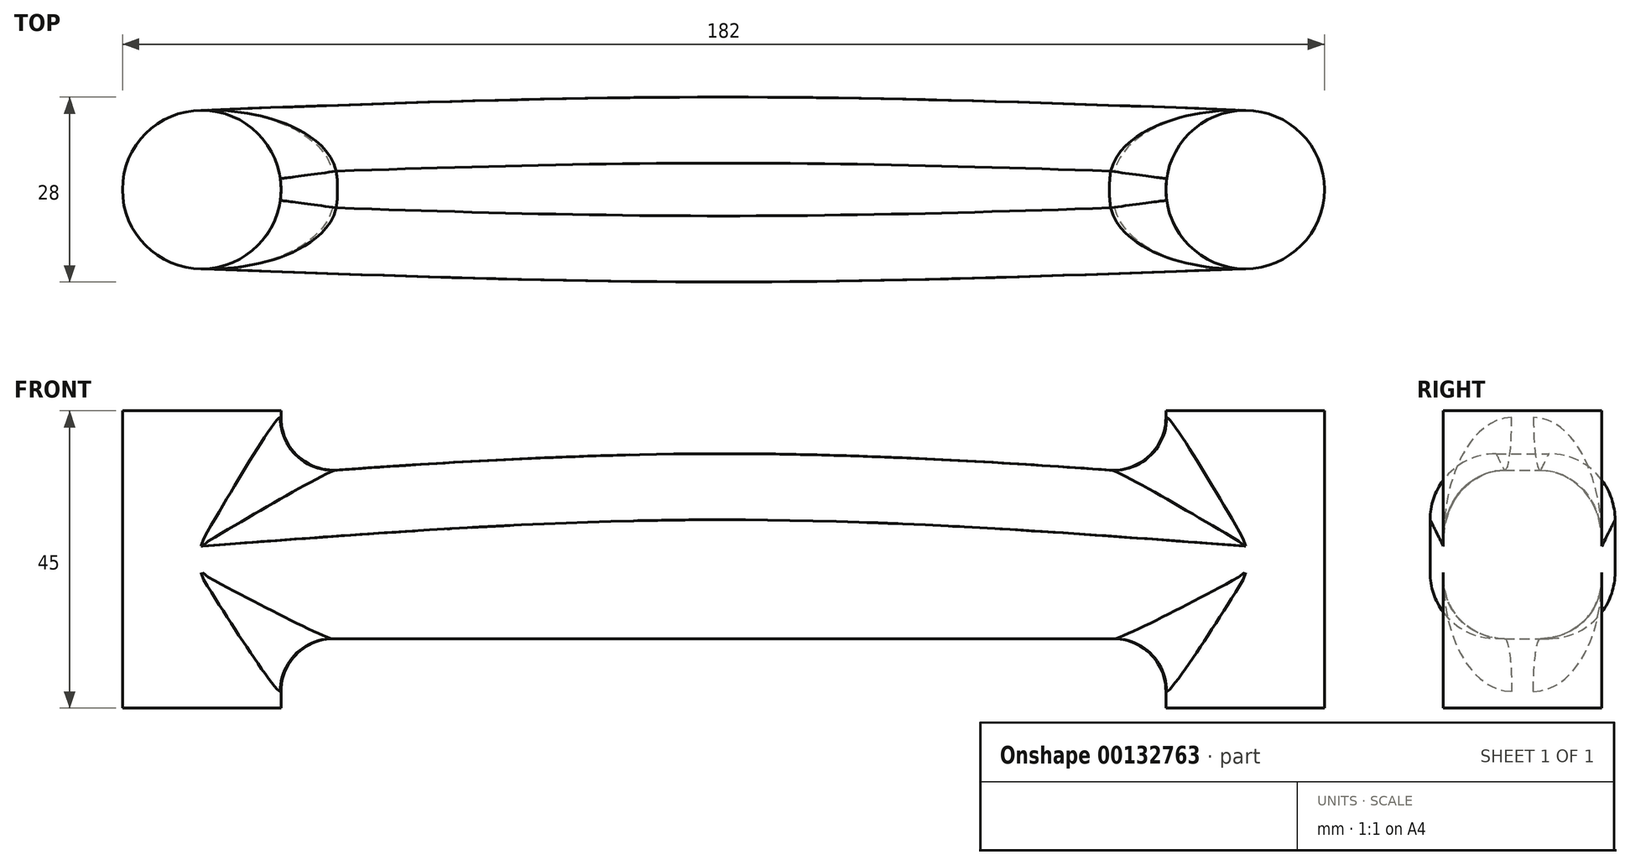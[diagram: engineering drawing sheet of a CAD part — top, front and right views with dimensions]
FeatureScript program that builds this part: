
annotation { "Feature Type Name" : "Feature", "Feature Type Description" : "" }
export const myFeature = defineFeature(function(context is Context, id is Id, definition is map)
    precondition{}
    {
        {
            var Q0;
            Q0=qCreatedBy(makeId("Top.planeOp"),FACE);
            var sketch = newSketch(context, id + "F0", { "sketchPlane" : qUnion([Q0])});
            skCircle(sketch, "E0", {"center": v(79, 0) * mm, "radius": 12 * mm});
            skLineSegment(sketch, "E1", {"start": v(-79, 0) * mm, "end": v(79, 0) * mm, "construction": true});
            skSolve(sketch);
        }
        {
            var Q0;
            Q0=makeQuery(id+"F0.imprint","IMPRINT",FACE,{"disambiguationData":[TD([[makeQuery(id+"F0.imprint","IMPRINT",EDGE,{"derivedFrom":sQuery(id+"F0.wireOp",EDGE,"6btjqJFc-xtUv-p354-ct1m-dMCtlRu3DlYN")}),1.0]])]});
            var Q1;
            Q1=makeQuery(id+"F0.imprint","IMPRINT",FACE,{"disambiguationData":[TD([[makeQuery(id+"F0.imprint","IMPRINT",EDGE,{"derivedFrom":sQuery(id+"F0.wireOp",EDGE,"E0")}),1.0]])]});
            extrude(context, id + "F1", {"entities" : qUnion([Q0, Q1]), "depth" : 45 * mm});
        }
        {
            var Q0;
            Q0=qCreatedBy(makeId("Right.planeOp"),FACE);
            cPlane(context, id + "F2", {"entities" : qUnion([Q0]), "cplaneType" : CPlaneType.OFFSET, "offset" : (158 / 2) * mm, "width" : 150 * mm, "height" : 150 * mm});
        }
        {
            var Q0;
            Q0=qCreatedBy(id+"F2.planeOp",FACE);
            var sketch = newSketch(context, id + "F3", { "sketchPlane" : qUnion([Q0])});
            skLineSegment(sketch, "E2.bottom", {"start": v(-12, 34.5) * mm, "end": v(12, 34.5) * mm});
            skLineSegment(sketch, "E2.top", {"start": v(-12, 10.5) * mm, "end": v(12, 10.5) * mm});
            skLineSegment(sketch, "E2.left", {"start": v(-12, 34.5) * mm, "end": v(-12, 10.5) * mm});
            skLineSegment(sketch, "E2.right", {"start": v(12, 34.5) * mm, "end": v(12, 10.5) * mm});
            skLineSegment(sketch, "E3", {"start": v(0, 10.5) * mm, "end": v(0, 0) * mm});
            skSolve(sketch);
        }
        {
            var Q0;
            Q0=qCreatedBy(makeId("Right.planeOp"),FACE);
            var sketch = newSketch(context, id + "F4", { "sketchPlane" : qUnion([Q0])});
            skLineSegment(sketch, "E4.bottom", {"start": v(-14, 38.5) * mm, "end": v(14, 38.5) * mm});
            skLineSegment(sketch, "E4.top", {"start": v(-14, 10.5) * mm, "end": v(14, 10.5) * mm});
            skLineSegment(sketch, "E4.left", {"start": v(-14, 38.5) * mm, "end": v(-14, 10.5) * mm});
            skLineSegment(sketch, "E4.right", {"start": v(14, 38.5) * mm, "end": v(14, 10.5) * mm});
            skLineSegment(sketch, "E5", {"start": v(0, 10.5) * mm, "end": v(0, 0) * mm});
            skSolve(sketch);
        }
        {
            var Q1;
            Q1=makeQuery(id+"F4.imprint","IMPRINT",FACE,{"disambiguationData":[TD([[makeQuery(id+"F4.imprint","IMPRINT",EDGE,{"derivedFrom":sQuery(id+"F4.wireOp",EDGE,"E4.bottom")}),-1.0]])]});
            var Q2;
            Q2=makeQuery(id+"F3.imprint","IMPRINT",FACE,{"disambiguationData":[TD([[makeQuery(id+"F3.imprint","IMPRINT",EDGE,{"derivedFrom":sQuery(id+"F3.wireOp",EDGE,"E2.bottom")}),-1.0]])]});
            loft(context, id + "F5", {"operationType" : NewBodyOperationType.ADD, "startCondition" : LoftEndDerivativeType.NORMAL_TO_PROFILE, "startMagnitude" : 1, "sheetProfilesArray" : [{ "sheetProfileEntities" : qUnion([Q1]) }, { "sheetProfileEntities" : qUnion([Q2]) }]});
        }
        {
            var Q0;
            Q0=makeQuery(id+"F5.opLoft","SWEPT_EDGE",EDGE,{"disambiguationData":[OSD([sQuery(id+"F3.wireOp",EDGE,"E2.bottom"),sQuery(id+"F3.wireOp",EDGE,"E2.right"),sQuery(id+"F4.wireOp",EDGE,"E4.bottom"),sQuery(id+"F4.wireOp",EDGE,"E4.right")])]});
            var Q1;
            Q1=makeQuery(id+"F5.opLoft","SWEPT_EDGE",EDGE,{"disambiguationData":[OSD([sQuery(id+"F3.wireOp",EDGE,"E2.bottom"),sQuery(id+"F3.wireOp",EDGE,"E2.left"),sQuery(id+"F4.wireOp",EDGE,"E4.bottom"),sQuery(id+"F4.wireOp",EDGE,"E4.left")])]});
            var Q2;
            Q2=makeQuery(id+"F5.opLoft","SWEPT_EDGE",EDGE,{"disambiguationData":[OSD([sQuery(id+"F3.wireOp",EDGE,"E2.top"),sQuery(id+"F3.wireOp",EDGE,"E2.right"),sQuery(id+"F4.wireOp",EDGE,"E4.top"),sQuery(id+"F4.wireOp",EDGE,"E4.right")])]});
            var Q3;
            Q3=makeQuery(id+"F5.opLoft","SWEPT_EDGE",EDGE,{"disambiguationData":[OSD([sQuery(id+"F3.wireOp",EDGE,"E2.top"),sQuery(id+"F3.wireOp",EDGE,"E2.left"),sQuery(id+"F4.wireOp",EDGE,"E4.top"),sQuery(id+"F4.wireOp",EDGE,"E4.left")])]});
            fillet(context, id + "F6", {"entities" : qUnion([Q0, Q1, Q2, Q3]), "radius" : 10 * mm, "tangentPropagation" : true, "allowEdgeOverflow" : false});
        }
        {
            var Q0;
            Q0=makeQuery(id+"F6.opFillet","BLEND_EDGE",EDGE,{"blendedFrom":[makeQuery(id+"F5.opLoft","SWEPT_EDGE",EDGE,{"disambiguationData":[OSD([sQuery(id+"F3.wireOp",EDGE,"E2.bottom"),sQuery(id+"F3.wireOp",EDGE,"E2.left"),sQuery(id+"F4.wireOp",EDGE,"E4.bottom"),sQuery(id+"F4.wireOp",EDGE,"E4.left")])]}),makeQuery(id+"F1.opExtrude","SWEPT_FACE",FACE,{"disambiguationData":[OSD([sQuery(id+"F0.wireOp",EDGE,"E0")])]})],"blendedInto":[makeQuery(id+"F1.opExtrude","SWEPT_FACE",FACE,{"disambiguationData":[OSD([sQuery(id+"F0.wireOp",EDGE,"E0")])]})]});
            var Q1;
            Q1=makeQuery(id+"F6.opFillet","BLEND_EDGE",EDGE,{"blendedFrom":[makeQuery(id+"F5.opLoft","SWEPT_EDGE",EDGE,{"disambiguationData":[OSD([sQuery(id+"F3.wireOp",EDGE,"E2.top"),sQuery(id+"F3.wireOp",EDGE,"E2.left"),sQuery(id+"F4.wireOp",EDGE,"E4.top"),sQuery(id+"F4.wireOp",EDGE,"E4.left")])]}),makeQuery(id+"F1.opExtrude","SWEPT_FACE",FACE,{"disambiguationData":[OSD([sQuery(id+"F0.wireOp",EDGE,"E0")])]})],"blendedInto":[makeQuery(id+"F1.opExtrude","SWEPT_FACE",FACE,{"disambiguationData":[OSD([sQuery(id+"F0.wireOp",EDGE,"E0")])]})]});
            fillet(context, id + "F7", {"entities" : qUnion([Q0, Q1]), "radius" : 8 * mm, "tangentPropagation" : true, "allowEdgeOverflow" : false});
        }
        {
            var Q0;
            Q0=makeQuery(id+"F1.opExtrude","SWEPT_BODY",BODY,{"disambiguationData":[OSD([sQuery(id+"F0.wireOp",EDGE,"E0")])]});
            var Q1;
            Q1=qCreatedBy(makeId("Right.planeOp"),FACE);
            mirror(context, id + "F8", {"operationType" : NewBodyOperationType.ADD, "entities" : qUnion([Q0]), "mirrorPlane" : qUnion([Q1])});
        }
    });
